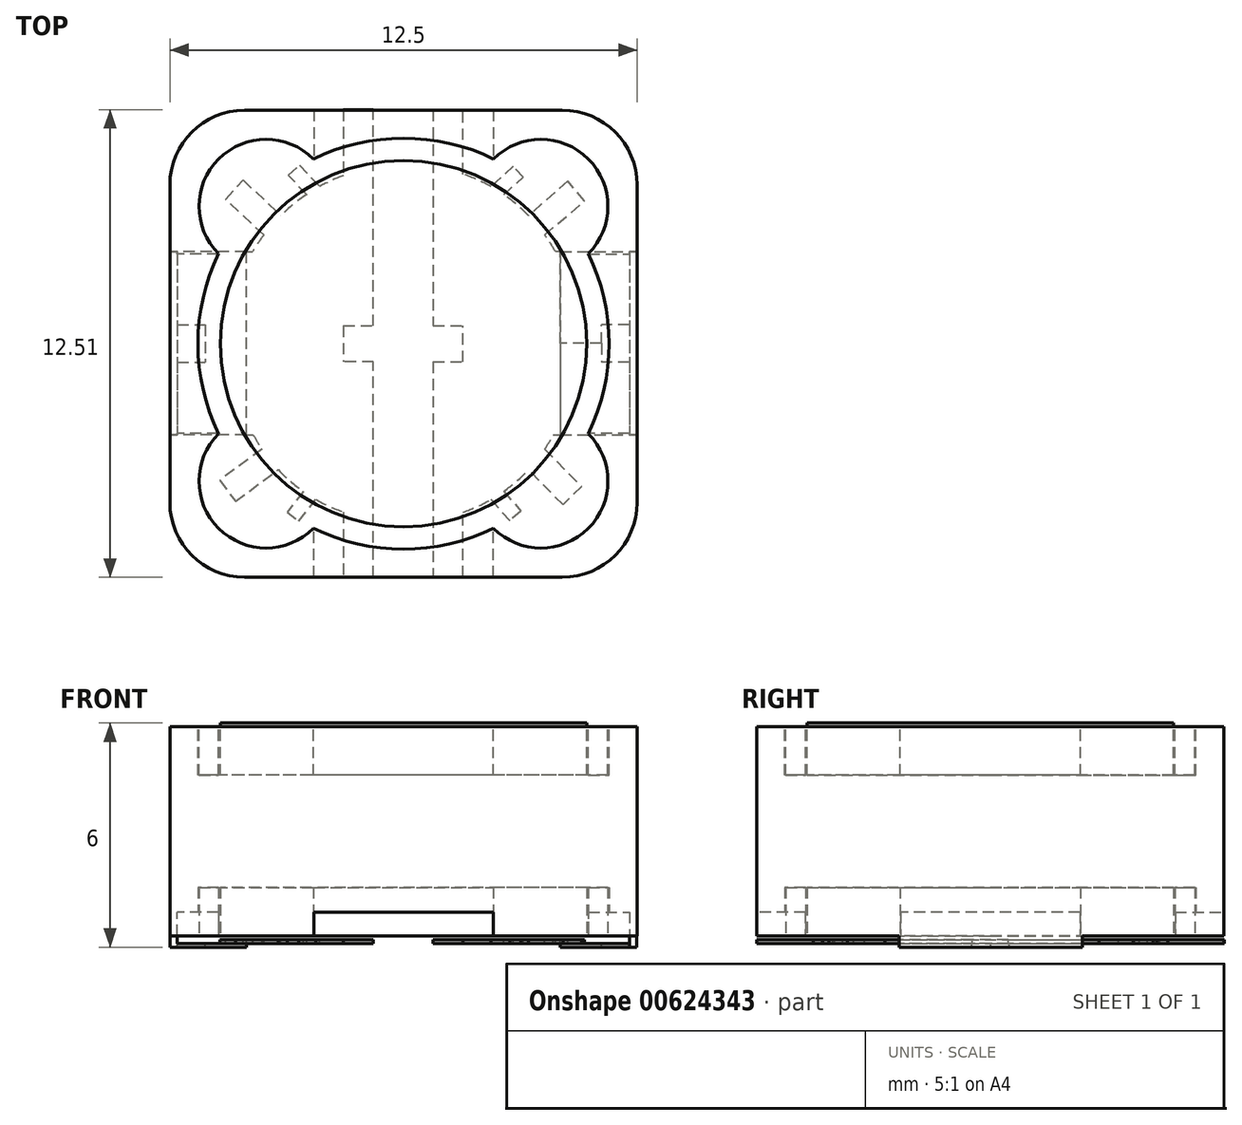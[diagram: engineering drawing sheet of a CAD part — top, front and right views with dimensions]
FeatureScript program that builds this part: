
annotation { "Feature Type Name" : "Feature", "Feature Type Description" : "" }
export const myFeature = defineFeature(function(context is Context, id is Id, definition is map)
    precondition{}
    {
        {
            var Q0;
            Q0=qCreatedBy(makeId("Top.planeOp"),FACE);
            var sketch = newSketch(context, id + "F0", { "sketchPlane" : qUnion([Q0])});
            skLineSegment(sketch, "E0.bottom", {"start": v(-4.25, 6.25) * mm, "end": v(4.25, 6.25) * mm});
            skLineSegment(sketch, "E0.top", {"start": v(-4.25, -6.25) * mm, "end": v(4.25, -6.25) * mm});
            skLineSegment(sketch, "E0.left", {"start": v(-6.25, 4.25) * mm, "end": v(-6.25, -4.25) * mm});
            skLineSegment(sketch, "E0.right", {"start": v(6.25, 4.25) * mm, "end": v(6.25, -4.25) * mm});
            skPoint(sketch, "E0.middle", {"position": v(0, 0) * mm});
            skPoint(sketch, "E1.visualSharp", {"position": v(-6.25, 6.25) * mm});
            skArc(sketch, "E1.filletArc", {"start": v(-4.25, 6.25) * mm, "mid": v(-5.66, 5.66) * mm, "end": v(-6.25, 4.25) * mm});
            skPoint(sketch, "E2.visualSharp", {"position": v(6.25, 6.25) * mm});
            skArc(sketch, "E2.filletArc", {"start": v(6.25, 4.25) * mm, "mid": v(5.66, 5.66) * mm, "end": v(4.25, 6.25) * mm});
            skPoint(sketch, "E3.visualSharp", {"position": v(6.25, -6.25) * mm});
            skArc(sketch, "E3.filletArc", {"start": v(4.25, -6.25) * mm, "mid": v(5.66, -5.66) * mm, "end": v(6.25, -4.25) * mm});
            skPoint(sketch, "E4.visualSharp", {"position": v(-6.25, -6.25) * mm});
            skArc(sketch, "E4.filletArc", {"start": v(-6.25, -4.25) * mm, "mid": v(-5.66, -5.66) * mm, "end": v(-4.25, -6.25) * mm});
            skSolve(sketch);
        }
        {
            var Q0;
            Q0=qCreatedBy(makeId("Top.planeOp"),FACE);
            var sketch = newSketch(context, id + "F1", { "sketchPlane" : qUnion([Q0])});
            skPoint(sketch, "E5.middle", {"position": v(0, 0) * mm});
            skCircle(sketch, "E6", {"center": v(0, 0) * mm, "radius": 5.5 * mm});
            skArc(sketch, "E7", {"start": v(-2.4, 4.94) * mm, "mid": v(-4.94, 4.94) * mm, "end": v(-4.94, 2.4) * mm});
            skArc(sketch, "E8", {"start": v(-4.94, -2.4) * mm, "mid": v(-4.94, -4.94) * mm, "end": v(-2.4, -4.94) * mm});
            skArc(sketch, "E9", {"start": v(2.4, -4.94) * mm, "mid": v(4.94, -4.94) * mm, "end": v(4.94, -2.4) * mm});
            skArc(sketch, "E10", {"start": v(4.94, 2.4) * mm, "mid": v(4.94, 4.94) * mm, "end": v(2.4, 4.94) * mm});
            skCircle(sketch, "E11", {"center": v(0, 0) * mm, "radius": 4.9 * mm});
            skSolve(sketch);
        }
        {
            var Q0;
            Q0 = qSketchRegion(id + "F0", true);
            extrude(context, id + "F2", {"entities" : qUnion([Q0]), "endBound" : BoundingType.SYMMETRIC, "depth" : 5.6 * mm, "offsetDistance" : 25 * mm});
        }
        {
            var Q0;
            Q0 = qSketchRegion(id + "F1", true);
            extrude(context, id + "F3", {"entities" : qUnion([Q0]), "operationType" : NewBodyOperationType.ADD, "endBound" : BoundingType.SYMMETRIC, "depth" : 6 * mm, "offsetDistance" : 25 * mm});
        }
        {
            var Q0;
            Q0=makeQuery(id+"F3.opExtrude","CAP_FACE",FACE,{"disambiguationData":[OSD([sQuery(id+"F1.wireOp",EDGE,"E6"),sQuery(id+"F1.wireOp",EDGE,"E7"),sQuery(id+"F1.wireOp",EDGE,"E8"),sQuery(id+"F1.wireOp",EDGE,"E9"),sQuery(id+"F1.wireOp",EDGE,"E10"),sQuery(id+"F1.wireOp",EDGE,"E11")])],"isStart":false});
            var Q1;
            Q1=makeQuery(id+"F3.opExtrude","CAP_FACE",FACE,{"disambiguationData":[OSD([sQuery(id+"F1.wireOp",EDGE,"E6"),sQuery(id+"F1.wireOp",EDGE,"E7"),sQuery(id+"F1.wireOp",EDGE,"E8"),sQuery(id+"F1.wireOp",EDGE,"E9"),sQuery(id+"F1.wireOp",EDGE,"E10"),sQuery(id+"F1.wireOp",EDGE,"E11")])],"isStart":true});
            extrude(context, id + "F4", {"entities" : qUnion([Q0, Q1]), "operationType" : NewBodyOperationType.REMOVE, "oppositeDirection" : true, "depth" : 1.5 * mm, "offsetDistance" : 25 * mm});
        }
        {
            var Q0;
            Q0=makeQuery(id+"F3.opExtrude","CAP_FACE",FACE,{"disambiguationData":[OSD([sQuery(id+"F1.wireOp",EDGE,"E6"),sQuery(id+"F1.wireOp",EDGE,"E7"),sQuery(id+"F1.wireOp",EDGE,"E8"),sQuery(id+"F1.wireOp",EDGE,"E9"),sQuery(id+"F1.wireOp",EDGE,"E10"),sQuery(id+"F1.wireOp",EDGE,"E11")])],"isStart":true});
            extrude(context, id + "F5", {"entities" : qUnion([Q0]), "operationType" : NewBodyOperationType.REMOVE, "oppositeDirection" : true, "depth" : 1.5 * mm, "offsetDistance" : 25 * mm});
        }
        {
            var Q0;
            Q0=qCreatedBy(makeId("Front.planeOp"),FACE);
            var sketch = newSketch(context, id + "F6", { "sketchPlane" : qUnion([Q0])});
            skLineSegment(sketch, "E12", {"start": v(2.5, -2.9) * mm, "end": v(2.5, -2.15) * mm});
            skLineSegment(sketch, "E13", {"start": v(2.5, -2.15) * mm, "end": v(-2.5, -2.15) * mm});
            skLineSegment(sketch, "E14", {"start": v(-2.5, -2.15) * mm, "end": v(-2.5, -2.9) * mm});
            skLineSegment(sketch, "E15", {"start": v(-2.5, -2.9) * mm, "end": v(2.5, -2.9) * mm});
            skSolve(sketch);
        }
        {
            var Q0;
            Q0=makeQuery(id+"F3.boolean.opBoolean","SPLIT",FACE,{"disambiguationData":[TD([makeQuery(id+"F3.opExtrude","SWEPT_FACE",FACE,{"disambiguationData":[OSD([sQuery(id+"F1.wireOp",EDGE,"E11")])]})])],"derivedFrom":makeQuery(id+"F2.opExtrude","CAP_FACE",FACE,{"disambiguationData":[OSD([sQuery(id+"F0.wireOp",EDGE,"E0.bottom"),sQuery(id+"F0.wireOp",EDGE,"E0.top"),sQuery(id+"F0.wireOp",EDGE,"E0.left"),sQuery(id+"F0.wireOp",EDGE,"E0.right"),sQuery(id+"F0.wireOp",EDGE,"E1.filletArc"),sQuery(id+"F0.wireOp",EDGE,"E2.filletArc"),sQuery(id+"F0.wireOp",EDGE,"E3.filletArc"),sQuery(id+"F0.wireOp",EDGE,"E4.filletArc")])],"isStart":false})});
            extrude(context, id + "F7", {"entities" : qUnion([Q0]), "operationType" : NewBodyOperationType.ADD, "depth" : 0.1 * mm, "offsetDistance" : 25 * mm});
        }
        {
            var Q0;
            Q0=makeQuery(id+"F6.imprint","IMPRINT",FACE,{"disambiguationData":[TD([[makeQuery(id+"F6.imprint","IMPRINT",EDGE,{"derivedFrom":sQuery(id+"F6.wireOp",EDGE,"E12")}),1.0]])]});
            cPlane(context, id + "F8", {"entities" : qUnion([Q0]), "cplaneType" : CPlaneType.OFFSET, "offset" : 6.25 * mm, "width" : 150 * mm, "height" : 150 * mm});
        }
        {
            var Q0;
            Q0=makeQuery(id+"F6.imprint","IMPRINT",FACE,{"disambiguationData":[TD([[makeQuery(id+"F6.imprint","IMPRINT",EDGE,{"derivedFrom":sQuery(id+"F6.wireOp",EDGE,"E12")}),1.0]])]});
            cPlane(context, id + "F9", {"entities" : qUnion([Q0]), "cplaneType" : CPlaneType.OFFSET, "offset" : 6.25 * mm, "oppositeDirection" : true, "width" : 150 * mm, "height" : 150 * mm});
        }
        {
            var Q0;
            Q0=qCreatedBy(id+"F8.planeOp",FACE);
            var sketch = newSketch(context, id + "F10", { "sketchPlane" : qUnion([Q0])});
            skLineSegment(sketch, "E16", {"start": v(0, -2.9) * mm, "end": v(2.4, -2.9) * mm});
            skLineSegment(sketch, "E17.bottom", {"start": v(2.4, -2.9) * mm, "end": v(-2.4, -2.9) * mm});
            skLineSegment(sketch, "E17.top", {"start": v(2.4, -2.16) * mm, "end": v(-2.4, -2.16) * mm});
            skLineSegment(sketch, "E17.left", {"start": v(2.4, -2.9) * mm, "end": v(2.4, -2.16) * mm});
            skLineSegment(sketch, "E17.right", {"start": v(-2.4, -2.9) * mm, "end": v(-2.4, -2.16) * mm});
            skSolve(sketch);
        }
        {
            var Q0;
            Q0=qCreatedBy(id+"F9.planeOp",FACE);
            var sketch = newSketch(context, id + "F11", { "sketchPlane" : qUnion([Q0])});
            skLineSegment(sketch, "E18", {"start": v(0, -2.9) * mm, "end": v(-2.4, -2.9) * mm});
            skLineSegment(sketch, "E19.bottom", {"start": v(-2.4, -2.9) * mm, "end": v(2.4, -2.9) * mm});
            skLineSegment(sketch, "E19.top", {"start": v(-2.4, -2.16) * mm, "end": v(2.4, -2.16) * mm});
            skLineSegment(sketch, "E19.left", {"start": v(-2.4, -2.9) * mm, "end": v(-2.4, -2.16) * mm});
            skLineSegment(sketch, "E19.right", {"start": v(2.4, -2.9) * mm, "end": v(2.4, -2.16) * mm});
            skSolve(sketch);
        }
        {
            var Q0;
            Q0=makeQuery(id+"F10.imprint","IMPRINT",FACE,{"disambiguationData":[TD([[makeQuery(id+"F10.imprint","IMPRINT",EDGE,{"derivedFrom":sQuery(id+"F10.wireOp",EDGE,"E17.top")}),1.0]])]});
            extrude(context, id + "F12", {"entities" : qUnion([Q0]), "operationType" : NewBodyOperationType.REMOVE, "oppositeDirection" : true, "depth" : 1.3 * mm, "offsetDistance" : 25 * mm});
        }
        {
            var Q0;
            Q0=makeQuery(id+"F11.imprint","IMPRINT",FACE,{"disambiguationData":[TD([[makeQuery(id+"F11.imprint","IMPRINT",EDGE,{"derivedFrom":sQuery(id+"F11.wireOp",EDGE,"E19.top")}),-1.0]])]});
            extrude(context, id + "F13", {"entities" : qUnion([Q0]), "operationType" : NewBodyOperationType.REMOVE, "depth" : 1.3 * mm, "offsetDistance" : 25 * mm});
        }
        {
            var Q0;
            Q0=qCreatedBy(makeId("Right.planeOp"),FACE);
            cPlane(context, id + "F14", {"entities" : qUnion([Q0]), "cplaneType" : CPlaneType.OFFSET, "offset" : 6.25 * mm, "width" : 150 * mm, "height" : 150 * mm});
        }
        {
            var Q0;
            Q0=qCreatedBy(id+"F14.planeOp",FACE);
            var sketch = newSketch(context, id + "F15", { "sketchPlane" : qUnion([Q0])});
            skLineSegment(sketch, "E20.bottom", {"start": v(2.4, -2.9) * mm, "end": v(2.4, -2.9) * mm});
            skLineSegment(sketch, "E21", {"start": v(2.4, -2.9) * mm, "end": v(2.4, -2.16) * mm});
            skLineSegment(sketch, "E22", {"start": v(-2.4, -2.9) * mm, "end": v(-2.4, -2.16) * mm});
            skLineSegment(sketch, "E23", {"start": v(-2.4, -2.16) * mm, "end": v(2.4, -2.16) * mm});
            skLineSegment(sketch, "E24", {"start": v(-2.4, -2.9) * mm, "end": v(2.4, -2.9) * mm});
            skSolve(sketch);
        }
        {
            var Q0;
            Q0=qCreatedBy(makeId("Right.planeOp"),FACE);
            cPlane(context, id + "F16", {"entities" : qUnion([Q0]), "cplaneType" : CPlaneType.OFFSET, "offset" : 6.25 * mm, "oppositeDirection" : true, "width" : 150 * mm, "height" : 150 * mm});
        }
        {
            var Q0;
            Q0=qCreatedBy(id+"F16.planeOp",FACE);
            var sketch = newSketch(context, id + "F17", { "sketchPlane" : qUnion([Q0])});
            skLineSegment(sketch, "E25", {"start": v(0, -2.9) * mm, "end": v(-2.4, -2.9) * mm});
            skLineSegment(sketch, "E26.bottom", {"start": v(-2.4, -2.9) * mm, "end": v(2.4, -2.9) * mm});
            skLineSegment(sketch, "E26.top", {"start": v(-2.4, -2.16) * mm, "end": v(2.4, -2.16) * mm});
            skLineSegment(sketch, "E26.left", {"start": v(-2.4, -2.9) * mm, "end": v(-2.4, -2.16) * mm});
            skLineSegment(sketch, "E26.right", {"start": v(2.4, -2.9) * mm, "end": v(2.4, -2.16) * mm});
            skSolve(sketch);
        }
        {
            var Q0;
            Q0=makeQuery(id+"F17.imprint","IMPRINT",FACE,{"disambiguationData":[TD([[makeQuery(id+"F17.imprint","IMPRINT",EDGE,{"derivedFrom":sQuery(id+"F17.wireOp",EDGE,"E26.top")}),-1.0]])]});
            extrude(context, id + "F18", {"entities" : qUnion([Q0]), "operationType" : NewBodyOperationType.REMOVE, "depth" : 1.3 * mm, "offsetDistance" : 25 * mm});
        }
        {
            var Q0;
            Q0=makeQuery(id+"F15.imprint","IMPRINT",FACE,{"disambiguationData":[TD([[makeQuery(id+"F15.imprint","IMPRINT",EDGE,{"derivedFrom":sQuery(id+"F15.wireOp",EDGE,"E21")}),1.0]])]});
            extrude(context, id + "F19", {"entities" : qUnion([Q0]), "operationType" : NewBodyOperationType.REMOVE, "oppositeDirection" : true, "depth" : 1.3 * mm, "offsetDistance" : 25 * mm});
        }
        {
            var Q0;
            Q0=qCreatedBy(makeId("Top.planeOp"),FACE);
            cPlane(context, id + "F20", {"entities" : qUnion([Q0]), "cplaneType" : CPlaneType.OFFSET, "offset" : 2.9 * mm, "oppositeDirection" : true, "width" : 150 * mm, "height" : 150 * mm});
        }
        {
            var Q0;
            Q0=qCreatedBy(id+"F20.planeOp",FACE);
            var sketch = newSketch(context, id + "F21", { "sketchPlane" : qUnion([Q0])});
            skLineSegment(sketch, "E27", {"start": v(-6.25, 0) * mm, "end": v(-6.25, -2.44) * mm});
            skLineSegment(sketch, "E28", {"start": v(6.24, -2.44) * mm, "end": v(6.24, 0) * mm});
            skLineSegment(sketch, "E29", {"start": v(-6.25, 0) * mm, "end": v(-6.25, 2.46) * mm});
            skLineSegment(sketch, "E30", {"start": v(6.24, 2.46) * mm, "end": v(6.24, 0) * mm});
            skLineSegment(sketch, "E31", {"start": v(-6.25, 0) * mm, "end": v(-4.2, 0) * mm});
            skLineSegment(sketch, "E32", {"start": v(-4.2, 0) * mm, "end": v(-4.2, -2.44) * mm});
            skLineSegment(sketch, "E33", {"start": v(-4.2, -2.44) * mm, "end": v(-6.25, -2.44) * mm});
            skLineSegment(sketch, "E34", {"start": v(-4.2, 0) * mm, "end": v(-4.2, 2.46) * mm});
            skLineSegment(sketch, "E35", {"start": v(-4.2, 2.46) * mm, "end": v(-6.25, 2.46) * mm});
            skLineSegment(sketch, "E36", {"start": v(6.24, 0) * mm, "end": v(4.2, 0) * mm});
            skLineSegment(sketch, "E37", {"start": v(4.2, -2.44) * mm, "end": v(6.24, -2.44) * mm});
            skLineSegment(sketch, "E38", {"start": v(4.2, 0) * mm, "end": v(4.2, 2.46) * mm});
            skLineSegment(sketch, "E39", {"start": v(4.2, 2.46) * mm, "end": v(6.24, 2.46) * mm});
            skLineSegment(sketch, "E40", {"start": v(-6.05, 2.46) * mm, "end": v(-6.05, -2.44) * mm});
            skLineSegment(sketch, "E41", {"start": v(6.04, 2.46) * mm, "end": v(6.04, -2.44) * mm});
            skLineSegment(sketch, "E42.bottom", {"start": v(-6.05, 0) * mm, "end": v(-5.3, 0) * mm});
            skLineSegment(sketch, "E42.top", {"start": v(-6.05, -0.5) * mm, "end": v(-5.3, -0.5) * mm});
            skLineSegment(sketch, "E42.left", {"start": v(-6.05, 0) * mm, "end": v(-6.05, -0.5) * mm});
            skLineSegment(sketch, "E42.right", {"start": v(-5.3, 0) * mm, "end": v(-5.3, -0.5) * mm});
            skLineSegment(sketch, "E43.top", {"start": v(-6.05, 0.5) * mm, "end": v(-5.3, 0.5) * mm});
            skLineSegment(sketch, "E43.left", {"start": v(-6.05, 0) * mm, "end": v(-6.05, 0.5) * mm});
            skLineSegment(sketch, "E43.right", {"start": v(-5.3, 0) * mm, "end": v(-5.3, 0.5) * mm});
            skLineSegment(sketch, "E44.bottom", {"start": v(6.04, 0) * mm, "end": v(5.3, 0) * mm});
            skLineSegment(sketch, "E44.top", {"start": v(6.04, -0.5) * mm, "end": v(5.3, -0.5) * mm});
            skLineSegment(sketch, "E44.left", {"start": v(6.04, 0) * mm, "end": v(6.04, -0.5) * mm});
            skLineSegment(sketch, "E44.right", {"start": v(5.3, 0) * mm, "end": v(5.3, -0.5) * mm});
            skLineSegment(sketch, "E45.top", {"start": v(6.04, 0.5) * mm, "end": v(5.3, 0.5) * mm});
            skLineSegment(sketch, "E45.left", {"start": v(6.04, 0) * mm, "end": v(6.04, 0.5) * mm});
            skLineSegment(sketch, "E45.right", {"start": v(5.3, 0) * mm, "end": v(5.3, 0.5) * mm});
            skLineSegment(sketch, "E46", {"start": v(-0.8, -6.24) * mm, "end": v(-0.8, 6.26) * mm});
            skLineSegment(sketch, "E47", {"start": v(-0.8, 6.26) * mm, "end": v(-1.6, 6.26) * mm});
            skLineSegment(sketch, "E48", {"start": v(-1.6, 6.26) * mm, "end": v(-1.6, -6.24) * mm});
            skLineSegment(sketch, "E49", {"start": v(1.6, -6.25) * mm, "end": v(1.6, 6.25) * mm});
            skLineSegment(sketch, "E50", {"start": v(1.6, 6.25) * mm, "end": v(0.8, 6.25) * mm});
            skLineSegment(sketch, "E51", {"start": v(0.8, 6.25) * mm, "end": v(0.8, -6.25) * mm});
            skArc(sketch, "E52", {"start": v(-4.02, -2.44) * mm, "mid": v(-2.68, -3.95) * mm, "end": v(-0.8, -4.7) * mm});
            skArc(sketch, "E53", {"start": v(1.6, -4.5) * mm, "mid": v(3, -3.7) * mm, "end": v(4, -2.44) * mm});
            skArc(sketch, "E54", {"start": v(4.07, 2.46) * mm, "mid": v(3.02, 3.73) * mm, "end": v(1.6, 4.54) * mm});
            skArc(sketch, "E55", {"start": v(-1.6, 4.5) * mm, "mid": v(-3, 3.69) * mm, "end": v(-4.04, 2.46) * mm});
            skLineSegment(sketch, "E56", {"start": v(-3.79, -2.82) * mm, "end": v(-4.91, -3.65) * mm});
            skLineSegment(sketch, "E57", {"start": v(-4.91, -3.65) * mm, "end": v(-4.5, -4.22) * mm});
            skLineSegment(sketch, "E58", {"start": v(-4.5, -4.22) * mm, "end": v(-3.35, -3.37) * mm});
            skLineSegment(sketch, "E59", {"start": v(-2.68, -3.95) * mm, "end": v(-3.11, -4.5) * mm});
            skLineSegment(sketch, "E60", {"start": v(-3.11, -4.5) * mm, "end": v(-2.8, -4.75) * mm});
            skLineSegment(sketch, "E61", {"start": v(-2.8, -4.75) * mm, "end": v(-2.34, -4.17) * mm});
            skLineSegment(sketch, "E62", {"start": v(3.78, -2.82) * mm, "end": v(4.76, -3.82) * mm});
            skLineSegment(sketch, "E63", {"start": v(4.76, -3.82) * mm, "end": v(4.27, -4.31) * mm});
            skLineSegment(sketch, "E64", {"start": v(4.27, -4.31) * mm, "end": v(3.35, -3.37) * mm});
            skLineSegment(sketch, "E65", {"start": v(2.68, -3.95) * mm, "end": v(3.14, -4.48) * mm});
            skLineSegment(sketch, "E66", {"start": v(3.14, -4.48) * mm, "end": v(2.84, -4.74) * mm});
            skLineSegment(sketch, "E67", {"start": v(2.84, -4.74) * mm, "end": v(2.34, -4.17) * mm});
            skLineSegment(sketch, "E68", {"start": v(3.78, 2.91) * mm, "end": v(4.85, 3.82) * mm});
            skLineSegment(sketch, "E69", {"start": v(4.85, 3.82) * mm, "end": v(4.4, 4.35) * mm});
            skLineSegment(sketch, "E70", {"start": v(4.4, 4.35) * mm, "end": v(3.35, 3.43) * mm});
            skLineSegment(sketch, "E71", {"start": v(2.68, 4) * mm, "end": v(3.2, 4.45) * mm});
            skLineSegment(sketch, "E72", {"start": v(3.2, 4.45) * mm, "end": v(2.94, 4.75) * mm});
            skLineSegment(sketch, "E73", {"start": v(2.94, 4.75) * mm, "end": v(2.34, 4.2) * mm});
            skLineSegment(sketch, "E74", {"start": v(-3.74, 2.91) * mm, "end": v(-4.76, 3.86) * mm});
            skLineSegment(sketch, "E75", {"start": v(-4.76, 3.86) * mm, "end": v(-4.29, 4.38) * mm});
            skLineSegment(sketch, "E76", {"start": v(-4.29, 4.38) * mm, "end": v(-3.28, 3.43) * mm});
            skLineSegment(sketch, "E77", {"start": v(-2.6, 4) * mm, "end": v(-3.08, 4.5) * mm});
            skLineSegment(sketch, "E78", {"start": v(-3.08, 4.5) * mm, "end": v(-2.78, 4.78) * mm});
            skLineSegment(sketch, "E79", {"start": v(-2.78, 4.78) * mm, "end": v(-2.24, 4.2) * mm});
            skLineSegment(sketch, "E80", {"start": v(-4.2, 2.46) * mm, "end": v(-4.04, 2.46) * mm});
            skLineSegment(sketch, "E81", {"start": v(-4.2, -2.44) * mm, "end": v(-4.02, -2.44) * mm});
            skLineSegment(sketch, "E82", {"start": v(4, -2.44) * mm, "end": v(4.2, -2.44) * mm});
            skLineSegment(sketch, "E83", {"start": v(4.2, 2.46) * mm, "end": v(4.07, 2.46) * mm});
            skLineSegment(sketch, "E84.bottom", {"start": v(0, 0) * mm, "end": v(-1.6, 0) * mm});
            skLineSegment(sketch, "E84.top", {"start": v(0, -0.48) * mm, "end": v(-1.6, -0.48) * mm});
            skLineSegment(sketch, "E84.left", {"start": v(0, 0) * mm, "end": v(0, -0.48) * mm});
            skLineSegment(sketch, "E84.right", {"start": v(-1.6, 0) * mm, "end": v(-1.6, -0.48) * mm});
            skLineSegment(sketch, "E85.bottom", {"start": v(0, 0) * mm, "end": v(1.6, 0) * mm});
            skLineSegment(sketch, "E85.top", {"start": v(0, -0.48) * mm, "end": v(1.6, -0.48) * mm});
            skLineSegment(sketch, "E85.right", {"start": v(1.6, 0) * mm, "end": v(1.6, -0.48) * mm});
            skLineSegment(sketch, "E86.bottom", {"start": v(-1.6, 0) * mm, "end": v(1.6, 0) * mm});
            skLineSegment(sketch, "E86.top", {"start": v(-1.6, 0.48) * mm, "end": v(1.6, 0.48) * mm});
            skLineSegment(sketch, "E86.left", {"start": v(-1.6, 0) * mm, "end": v(-1.6, 0.48) * mm});
            skLineSegment(sketch, "E86.right", {"start": v(1.6, 0) * mm, "end": v(1.6, 0.48) * mm});
            skLineSegment(sketch, "E87.bottom", {"start": v(-0.47, 0) * mm, "end": v(0.52, 0) * mm});
            skLineSegment(sketch, "E87.top", {"start": v(-0.47, 0) * mm, "end": v(0.52, 0) * mm});
            skLineSegment(sketch, "E87.left", {"start": v(-0.47, 0) * mm, "end": v(-0.47, 0) * mm});
            skLineSegment(sketch, "E87.right", {"start": v(0.52, 0) * mm, "end": v(0.52, 0) * mm});
            skLineSegment(sketch, "E88.bottom", {"start": v(1.2, 0) * mm, "end": v(-1.16, 0) * mm});
            skLineSegment(sketch, "E88.top", {"start": v(1.2, 0) * mm, "end": v(-1.16, 0) * mm});
            skLineSegment(sketch, "E88.left", {"start": v(1.2, 0) * mm, "end": v(1.2, 0) * mm});
            skLineSegment(sketch, "E88.right", {"start": v(-1.16, 0) * mm, "end": v(-1.16, 0) * mm});
            skLineSegment(sketch, "E89", {"start": v(-1.6, -6.24) * mm, "end": v(-0.8, -6.24) * mm});
            skLineSegment(sketch, "E90", {"start": v(0.8, -6.25) * mm, "end": v(1.6, -6.25) * mm});
            skLineSegment(sketch, "E91", {"start": v(4.2, 0) * mm, "end": v(4.2, -2.44) * mm});
            skSolve(sketch);
        }
        {
            var Q0;
            {var subQ0=sQuery(id+"F21.wireOp",EDGE,"E27");Q0=makeQuery(id+"F21.imprint","IMPRINT",FACE,{"disambiguationData":[TD([[makeQuery(id+"F21.imprint","IMPRINT",EDGE,{"derivedFrom":subQ0}),1.0]])]});}
            var Q1;
            {var subQ0=sQuery(id+"F21.wireOp",EDGE,"E29");Q1=makeQuery(id+"F21.imprint","IMPRINT",FACE,{"disambiguationData":[TD([[makeQuery(id+"F21.imprint","IMPRINT",EDGE,{"derivedFrom":subQ0}),-1.0]])]});}
            var Q2;
            {var subQ0=sQuery(id+"F21.wireOp",EDGE,"E28");Q2=makeQuery(id+"F21.imprint","IMPRINT",FACE,{"disambiguationData":[TD([[makeQuery(id+"F21.imprint","IMPRINT",EDGE,{"derivedFrom":subQ0}),1.0]])]});}
            var Q3;
            {var subQ0=sQuery(id+"F21.wireOp",EDGE,"E30");Q3=makeQuery(id+"F21.imprint","IMPRINT",FACE,{"disambiguationData":[TD([[makeQuery(id+"F21.imprint","IMPRINT",EDGE,{"derivedFrom":subQ0}),-1.0]])]});}
            extrude(context, id + "F22", {"entities" : qUnion([Q0, Q1, Q2, Q3]), "operationType" : NewBodyOperationType.ADD, "depth" : 0.74 * mm, "offsetDistance" : 25 * mm});
        }
        {
            var Q0;
            Q0=makeQuery(id+"F22.opExtrude","CAP_FACE",FACE,{"disambiguationData":[OSD([sQuery(id+"F21.wireOp",EDGE,"E27"),sQuery(id+"F21.wireOp",EDGE,"E29"),sQuery(id+"F21.wireOp",EDGE,"E33"),sQuery(id+"F21.wireOp",EDGE,"E35"),sQuery(id+"F21.wireOp",EDGE,"E40")])],"isStart":true});
            var Q1;
            Q1=makeQuery(id+"F22.opExtrude","CAP_FACE",FACE,{"disambiguationData":[OSD([sQuery(id+"F21.wireOp",EDGE,"E28"),sQuery(id+"F21.wireOp",EDGE,"E30"),sQuery(id+"F21.wireOp",EDGE,"E37"),sQuery(id+"F21.wireOp",EDGE,"E39"),sQuery(id+"F21.wireOp",EDGE,"E41")])],"isStart":true});
            extrude(context, id + "F23", {"entities" : qUnion([Q0, Q1]), "operationType" : NewBodyOperationType.ADD, "depth" : 0.2 * mm, "offsetDistance" : 25 * mm});
        }
        {
            var Q0;
            {var subQ0=sQuery(id+"F21.wireOp",EDGE,"E32");Q0=makeQuery(id+"F21.imprint","IMPRINT",FACE,{"disambiguationData":[TD([[makeQuery(id+"F21.imprint","IMPRINT",EDGE,{"derivedFrom":subQ0}),-1.0]])]});}
            var Q1;
            {var subQ0=sQuery(id+"F21.wireOp",EDGE,"E34");Q1=makeQuery(id+"F21.imprint","IMPRINT",FACE,{"disambiguationData":[TD([[makeQuery(id+"F21.imprint","IMPRINT",EDGE,{"derivedFrom":subQ0}),1.0]])]});}
            var Q2;
            {var subQ0=sQuery(id+"F21.wireOp",EDGE,"F9xKnShF-xsFI-T3vn-fbI8-78K1E03DxVts");Q2=makeQuery(id+"F21.imprint","IMPRINT",FACE,{"disambiguationData":[TD([[makeQuery(id+"F21.imprint","IMPRINT",EDGE,{"derivedFrom":subQ0}),1.0]])]});}
            var Q3;
            {var subQ0=sQuery(id+"F21.wireOp",EDGE,"E38");Q3=makeQuery(id+"F21.imprint","IMPRINT",FACE,{"disambiguationData":[TD([[makeQuery(id+"F21.imprint","IMPRINT",EDGE,{"derivedFrom":subQ0}),-1.0]])]});}
            extrude(context, id + "F24", {"entities" : qUnion([Q0, Q1, Q2, Q3]), "operationType" : NewBodyOperationType.ADD, "oppositeDirection" : true, "depth" : 0.2 * mm, "offsetDistance" : 25 * mm});
        }
        {
            var Q0;
            {var subQ0=sQuery(id+"F21.wireOp",EDGE,"E32");Q0=makeQuery(id+"F21.imprint","IMPRINT",FACE,{"disambiguationData":[TD([[makeQuery(id+"F21.imprint","IMPRINT",EDGE,{"derivedFrom":subQ0}),-1.0]])]});}
            var Q1;
            {var subQ0=sQuery(id+"F21.wireOp",EDGE,"E34");Q1=makeQuery(id+"F21.imprint","IMPRINT",FACE,{"disambiguationData":[TD([[makeQuery(id+"F21.imprint","IMPRINT",EDGE,{"derivedFrom":subQ0}),1.0]])]});}
            var Q2;
            {var subQ0=sQuery(id+"F21.wireOp",EDGE,"F9xKnShF-xsFI-T3vn-fbI8-78K1E03DxVts");Q2=makeQuery(id+"F21.imprint","IMPRINT",FACE,{"disambiguationData":[TD([[makeQuery(id+"F21.imprint","IMPRINT",EDGE,{"derivedFrom":subQ0}),1.0]])]});}
            var Q3;
            {var subQ0=sQuery(id+"F21.wireOp",EDGE,"E38");Q3=makeQuery(id+"F21.imprint","IMPRINT",FACE,{"disambiguationData":[TD([[makeQuery(id+"F21.imprint","IMPRINT",EDGE,{"derivedFrom":subQ0}),-1.0]])]});}
            extrude(context, id + "F25", {"entities" : qUnion([Q0, Q1, Q2, Q3]), "operationType" : NewBodyOperationType.REMOVE, "oppositeDirection" : true, "depth" : 0.1 * mm, "offsetDistance" : 25 * mm});
        }
        {
            var Q0;
            Q0=makeQuery(id+"F21.imprint","IMPRINT",FACE,{"disambiguationData":[TD([[makeQuery(id+"F21.imprint","IMPRINT",EDGE,{"derivedFrom":sQuery(id+"F21.wireOp",EDGE,"E44.top")}),-1.0]])]});
            var Q1;
            Q1=makeQuery(id+"F21.imprint","IMPRINT",FACE,{"disambiguationData":[TD([[makeQuery(id+"F21.imprint","IMPRINT",EDGE,{"derivedFrom":sQuery(id+"F21.wireOp",EDGE,"E44.bottom")}),-1.0]])]});
            var Q2;
            Q2=makeQuery(id+"F21.imprint","IMPRINT",FACE,{"disambiguationData":[TD([[makeQuery(id+"F21.imprint","IMPRINT",EDGE,{"derivedFrom":sQuery(id+"F21.wireOp",EDGE,"E42.top")}),1.0]])]});
            var Q3;
            Q3=makeQuery(id+"F21.imprint","IMPRINT",FACE,{"disambiguationData":[TD([[makeQuery(id+"F21.imprint","IMPRINT",EDGE,{"derivedFrom":sQuery(id+"F21.wireOp",EDGE,"E42.bottom")}),1.0]])]});
            extrude(context, id + "F26", {"entities" : qUnion([Q0, Q1, Q2, Q3]), "operationType" : NewBodyOperationType.REMOVE, "depth" : 0.2 * mm, "offsetDistance" : 25 * mm});
        }
        {
            var Q0;
            {var subQ0=sQuery(id+"F21.wireOp",EDGE,"E62");Q0=makeQuery(id+"F21.imprint","IMPRINT",FACE,{"disambiguationData":[TD([[makeQuery(id+"F21.imprint","IMPRINT",EDGE,{"derivedFrom":subQ0}),-1.0]])]});}
            var Q1;
            Q1=makeQuery(id+"F21.imprint","IMPRINT",FACE,{"disambiguationData":[TD([[makeQuery(id+"F21.imprint","IMPRINT",EDGE,{"derivedFrom":sQuery(id+"F21.wireOp",EDGE,"E38")}),1.0]])]});
            var Q2;
            {var subQ5=sQuery(id+"F21.wireOp",EDGE,"E90");Q2=makeQuery(id+"F21.imprint","IMPRINT",FACE,{"disambiguationData":[TD([[makeQuery(id+"F21.imprint","IMPRINT",EDGE,{"derivedFrom":subQ5}),1.0]])]});}
            var Q3;
            {var subQ0=sQuery(id+"F21.wireOp",EDGE,"E89");Q3=makeQuery(id+"F21.imprint","IMPRINT",FACE,{"disambiguationData":[TD([[makeQuery(id+"F21.imprint","IMPRINT",EDGE,{"derivedFrom":subQ0}),1.0]])]});}
            var Q4;
            {var subQ0=sQuery(id+"F21.wireOp",EDGE,"E52");var subQ1=sQuery(id+"F21.wireOp",EDGE,"E46");var subQ2=makeQuery(id+"F21.imprint","INTERSECT",VERTEX,{"derivedFrom":[subQ1,subQ0]});Q4=makeQuery(id+"F21.imprint","IMPRINT",FACE,{"disambiguationData":[TD([[makeQuery(id+"F21.imprint","IMPRINT",EDGE,{"disambiguationData":[TD([[subQ2,-1.0]])],"derivedFrom":subQ1}),1.0]])]});}
            var Q5;
            Q5=makeQuery(id+"F21.imprint","IMPRINT",FACE,{"disambiguationData":[TD([[makeQuery(id+"F21.imprint","IMPRINT",EDGE,{"derivedFrom":sQuery(id+"F21.wireOp",EDGE,"E32")}),1.0]])]});
            var Q6;
            {var subQ0=sQuery(id+"F21.wireOp",EDGE,"E56");Q6=makeQuery(id+"F21.imprint","IMPRINT",FACE,{"disambiguationData":[TD([[makeQuery(id+"F21.imprint","IMPRINT",EDGE,{"derivedFrom":subQ0}),1.0]])]});}
            var Q7;
            {var subQ0=sQuery(id+"F21.wireOp",EDGE,"E74");Q7=makeQuery(id+"F21.imprint","IMPRINT",FACE,{"disambiguationData":[TD([[makeQuery(id+"F21.imprint","IMPRINT",EDGE,{"derivedFrom":subQ0}),-1.0]])]});}
            var Q8;
            {var subQ0=sQuery(id+"F21.wireOp",EDGE,"E68");Q8=makeQuery(id+"F21.imprint","IMPRINT",FACE,{"disambiguationData":[TD([[makeQuery(id+"F21.imprint","IMPRINT",EDGE,{"derivedFrom":subQ0}),1.0]])]});}
            var Q9;
            {var subQ0=sQuery(id+"F21.wireOp",EDGE,"E71");Q9=makeQuery(id+"F21.imprint","IMPRINT",FACE,{"disambiguationData":[TD([[makeQuery(id+"F21.imprint","IMPRINT",EDGE,{"derivedFrom":subQ0}),1.0]])]});}
            var Q10;
            {var subQ0=sQuery(id+"F21.wireOp",EDGE,"E77");Q10=makeQuery(id+"F21.imprint","IMPRINT",FACE,{"disambiguationData":[TD([[makeQuery(id+"F21.imprint","IMPRINT",EDGE,{"derivedFrom":subQ0}),-1.0]])]});}
            var Q11;
            {var subQ4=sQuery(id+"F21.wireOp",EDGE,"E47");Q11=makeQuery(id+"F21.imprint","IMPRINT",FACE,{"disambiguationData":[TD([[makeQuery(id+"F21.imprint","IMPRINT",EDGE,{"derivedFrom":subQ4}),1.0]])]});}
            var Q12;
            {var subQ1=sQuery(id+"F21.wireOp",EDGE,"E50");Q12=makeQuery(id+"F21.imprint","IMPRINT",FACE,{"disambiguationData":[TD([[makeQuery(id+"F21.imprint","IMPRINT",EDGE,{"derivedFrom":subQ1}),1.0]])]});}
            var Q13;
            {var subQ0=sQuery(id+"F21.wireOp",EDGE,"E65");Q13=makeQuery(id+"F21.imprint","IMPRINT",FACE,{"disambiguationData":[TD([[makeQuery(id+"F21.imprint","IMPRINT",EDGE,{"derivedFrom":subQ0}),-1.0]])]});}
            var Q14;
            {var subQ0=sQuery(id+"F21.wireOp",EDGE,"E59");Q14=makeQuery(id+"F21.imprint","IMPRINT",FACE,{"disambiguationData":[TD([[makeQuery(id+"F21.imprint","IMPRINT",EDGE,{"derivedFrom":subQ0}),1.0]])]});}
            var Q15;
            {var subQ1=sQuery(id+"F21.wireOp",EDGE,"E84.right");Q15=makeQuery(id+"F21.imprint","IMPRINT",FACE,{"disambiguationData":[TD([[makeQuery(id+"F21.imprint","IMPRINT",EDGE,{"derivedFrom":subQ1}),1.0]])]});}
            var Q16;
            {var subQ0=sQuery(id+"F21.wireOp",EDGE,"E86.left");Q16=makeQuery(id+"F21.imprint","IMPRINT",FACE,{"disambiguationData":[TD([[makeQuery(id+"F21.imprint","IMPRINT",EDGE,{"derivedFrom":subQ0}),-1.0]])]});}
            var Q17;
            {var subQ1=sQuery(id+"F21.wireOp",EDGE,"E85.right");Q17=makeQuery(id+"F21.imprint","IMPRINT",FACE,{"disambiguationData":[TD([[makeQuery(id+"F21.imprint","IMPRINT",EDGE,{"derivedFrom":subQ1}),-1.0]])]});}
            var Q18;
            {var subQ0=sQuery(id+"F21.wireOp",EDGE,"E86.right");Q18=makeQuery(id+"F21.imprint","IMPRINT",FACE,{"disambiguationData":[TD([[makeQuery(id+"F21.imprint","IMPRINT",EDGE,{"derivedFrom":subQ0}),1.0]])]});}
            extrude(context, id + "F27", {"entities" : qUnion([Q0, Q1, Q2, Q3, Q4, Q5, Q6, Q7, Q8, Q9, Q10, Q11, Q12, Q13, Q14, Q15, Q16, Q17, Q18]), "oppositeDirection" : true, "depth" : 0.1 * mm, "offsetDistance" : 25 * mm});
        }
        {
            var Q0;
            {var subQ1=sQuery(id+"F21.wireOp",EDGE,"E84.left");Q0=makeQuery(id+"F21.imprint","IMPRINT",FACE,{"disambiguationData":[TD([[makeQuery(id+"F21.imprint","IMPRINT",EDGE,{"derivedFrom":subQ1}),-1.0]])]});}
            var Q1;
            {var subQ1=sQuery(id+"F21.wireOp",EDGE,"E85.right");Q1=makeQuery(id+"F21.imprint","IMPRINT",FACE,{"disambiguationData":[TD([[makeQuery(id+"F21.imprint","IMPRINT",EDGE,{"derivedFrom":subQ1}),-1.0]])]});}
            var Q2;
            {var subQ5=sQuery(id+"F21.wireOp",EDGE,"E84.left");Q2=makeQuery(id+"F21.imprint","IMPRINT",FACE,{"disambiguationData":[TD([[makeQuery(id+"F21.imprint","IMPRINT",EDGE,{"derivedFrom":subQ5}),1.0]])]});}
            var Q3;
            {var subQ1=sQuery(id+"F21.wireOp",EDGE,"E84.right");Q3=makeQuery(id+"F21.imprint","IMPRINT",FACE,{"disambiguationData":[TD([[makeQuery(id+"F21.imprint","IMPRINT",EDGE,{"derivedFrom":subQ1}),1.0]])]});}
            var Q4;
            {var subQ3=sQuery(id+"F21.wireOp",EDGE,"E88.top");var subQ5=makeQuery(id+"F21.imprint","IMPRINT",VERTEX,{"disambiguationData":[OD(0.0)],"derivedFrom":subQ3});Q4=makeQuery(id+"F21.imprint","IMPRINT",FACE,{"disambiguationData":[TD([[makeQuery(id+"F21.imprint","IMPRINT",EDGE,{"disambiguationData":[TD([[subQ5,1.0]])],"derivedFrom":subQ3}),-1.0]])]});}
            var Q5;
            {var subQ0=sQuery(id+"F21.wireOp",EDGE,"E86.right");Q5=makeQuery(id+"F21.imprint","IMPRINT",FACE,{"disambiguationData":[TD([[makeQuery(id+"F21.imprint","IMPRINT",EDGE,{"derivedFrom":subQ0}),1.0]])]});}
            var Q6;
            {var subQ0=sQuery(id+"F21.wireOp",EDGE,"E86.left");Q6=makeQuery(id+"F21.imprint","IMPRINT",FACE,{"disambiguationData":[TD([[makeQuery(id+"F21.imprint","IMPRINT",EDGE,{"derivedFrom":subQ0}),-1.0]])]});}
            extrude(context, id + "F28", {"entities" : qUnion([Q0, Q1, Q2, Q3, Q4, Q5, Q6]), "operationType" : NewBodyOperationType.REMOVE, "oppositeDirection" : true, "depth" : 0.1 * mm, "offsetDistance" : 25 * mm});
        }
        {
            var Q0;
            {var subQ0=sQuery(id+"F21.wireOp",EDGE,"E44.top");Q0=makeQuery(id+"F21.imprint","IMPRINT",FACE,{"disambiguationData":[TD([[makeQuery(id+"F21.imprint","IMPRINT",EDGE,{"derivedFrom":subQ0}),1.0]])]});}
            extrude(context, id + "F29", {"entities" : qUnion([Q0]), "oppositeDirection" : true, "depth" : 0.2 * mm, "offsetDistance" : 25 * mm});
        }
        {
            var Q0;
            {var subQ0=sQuery(id+"F21.wireOp",EDGE,"E44.top");Q0=makeQuery(id+"F21.imprint","IMPRINT",FACE,{"disambiguationData":[TD([[makeQuery(id+"F21.imprint","IMPRINT",EDGE,{"derivedFrom":subQ0}),1.0]])]});}
            extrude(context, id + "F30", {"entities" : qUnion([Q0]), "operationType" : NewBodyOperationType.REMOVE, "oppositeDirection" : true, "depth" : 0.1 * mm, "offsetDistance" : 25 * mm});
        }
    });
